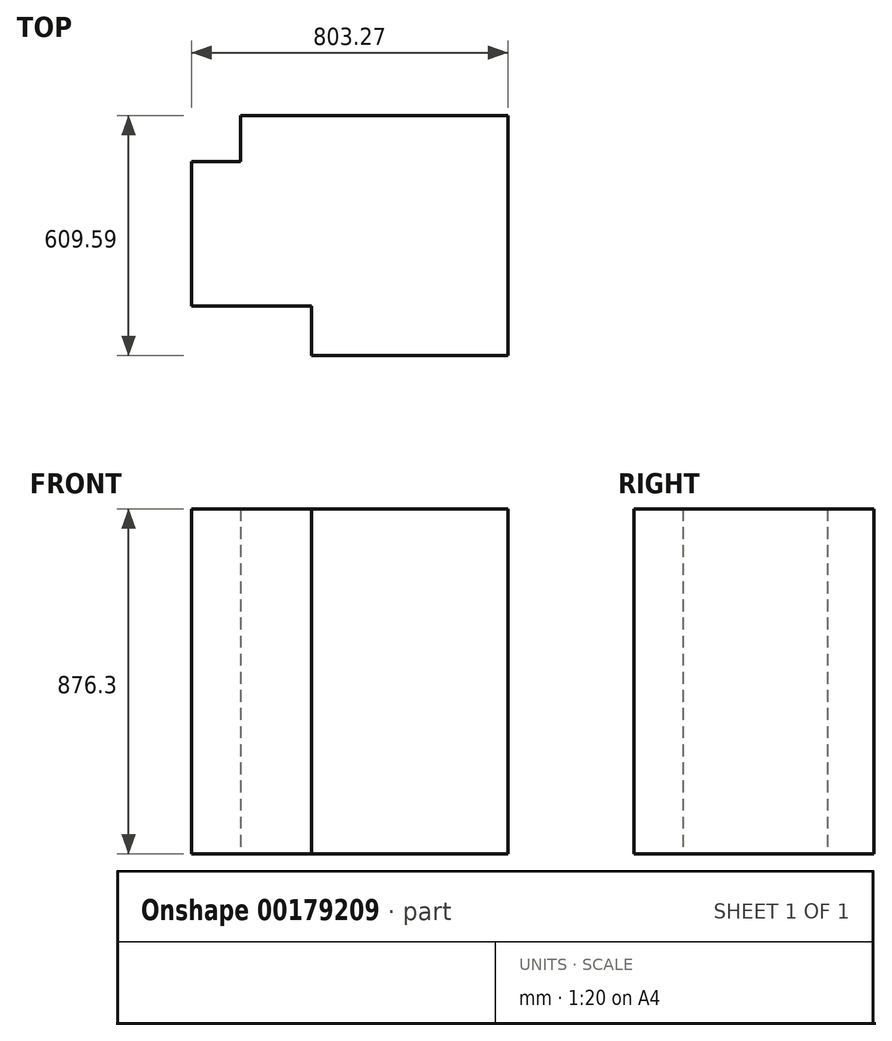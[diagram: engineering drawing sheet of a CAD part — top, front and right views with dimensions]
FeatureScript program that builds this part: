
annotation { "Feature Type Name" : "Feature", "Feature Type Description" : "" }
export const myFeature = defineFeature(function(context is Context, id is Id, definition is map)
    precondition{}
    {
        {
            var Q0;
            Q0=qCreatedBy(makeId("Top.planeOp"),FACE);
            var sketch = newSketch(context, id + "F0", { "sketchPlane" : qUnion([Q0])});
            skLineSegment(sketch, "E0.bottom", {"start": v(123.83, 117.47) * mm, "end": v(803.28, 117.47) * mm});
            skLineSegment(sketch, "E0.top", {"start": v(304.8, -492.13) * mm, "end": v(803.28, -492.13) * mm});
            skLineSegment(sketch, "E0.right", {"start": v(803.28, 117.48) * mm, "end": v(803.28, -492.13) * mm});
            skLineSegment(sketch, "E1", {"start": v(123.83, 117.47) * mm, "end": v(123.83, 0) * mm});
            skLineSegment(sketch, "E2", {"start": v(123.83, 0) * mm, "end": v(0, 0) * mm});
            skLineSegment(sketch, "E3", {"start": v(0, 0) * mm, "end": v(0, -366.71) * mm});
            skLineSegment(sketch, "E4", {"start": v(0, -366.71) * mm, "end": v(304.8, -366.71) * mm});
            skLineSegment(sketch, "E5", {"start": v(304.8, -366.71) * mm, "end": v(304.8, -492.13) * mm});
            skSolve(sketch);
        }
        {
            var Q0;
            Q0=makeQuery(id+"F0.imprint","IMPRINT",FACE,{"disambiguationData":[TD([[makeQuery(id+"F0.imprint","IMPRINT",EDGE,{"derivedFrom":sQuery(id+"F0.wireOp",EDGE,"E0.bottom")}),-1.0]])]});
            extrude(context, id + "F1", {"entities" : qUnion([Q0]), "depth" : 876.3 * mm});
        }
    });
